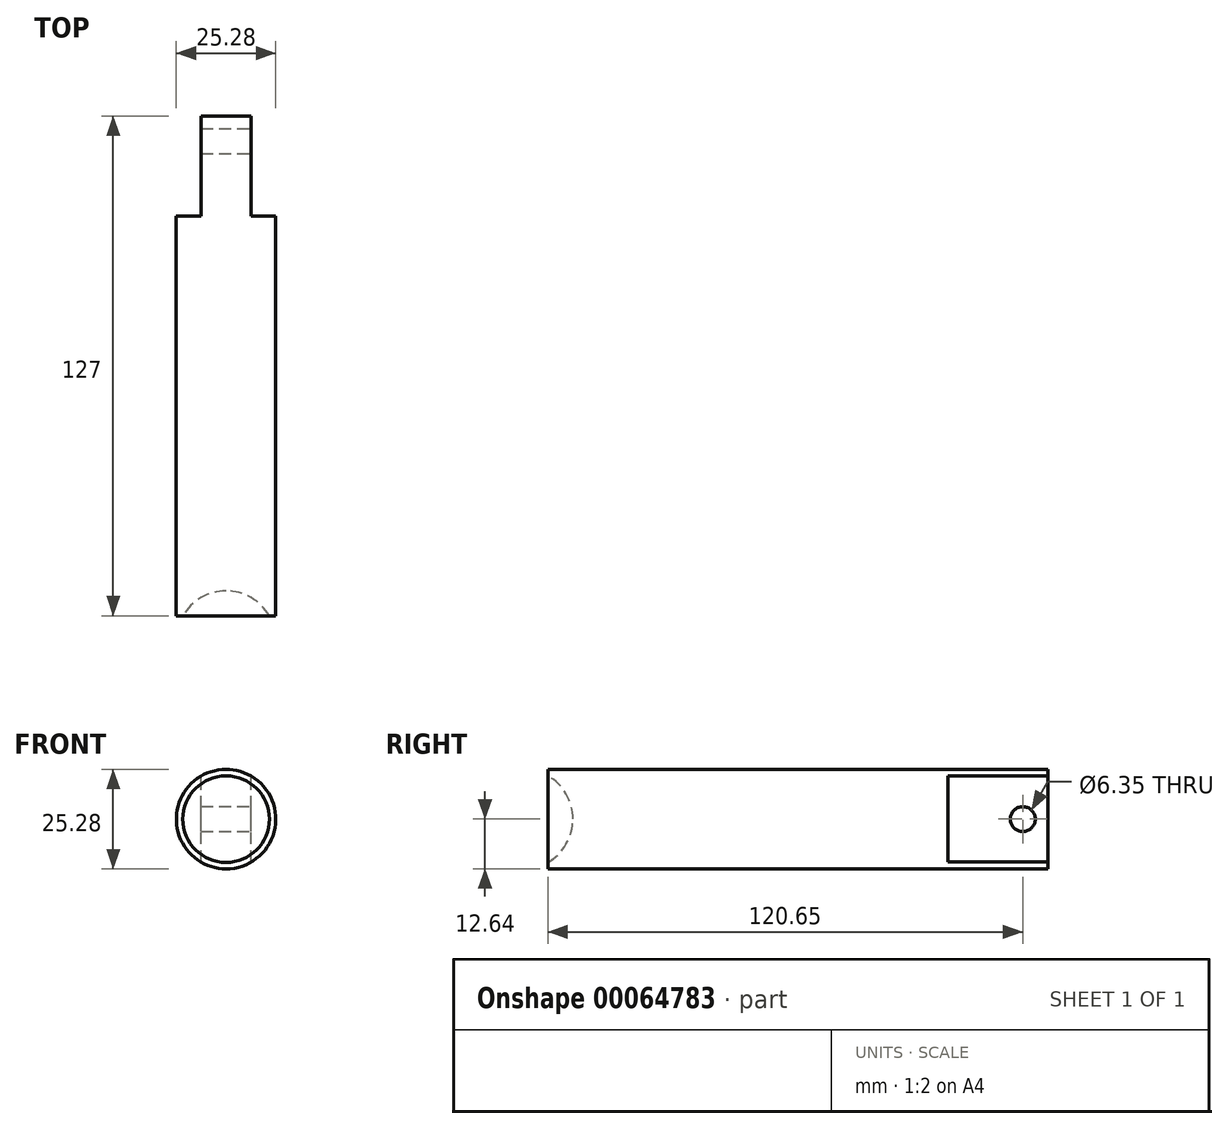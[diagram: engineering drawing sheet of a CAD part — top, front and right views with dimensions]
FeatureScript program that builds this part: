
annotation { "Feature Type Name" : "Feature", "Feature Type Description" : "" }
export const myFeature = defineFeature(function(context is Context, id is Id, definition is map)
    precondition{}
    {
        {
            var Q0;
            Q0=qCreatedBy(makeId("Front.planeOp"),FACE);
            var sketch = newSketch(context, id + "F0", { "sketchPlane" : qUnion([Q0])});
            skCircle(sketch, "E0", {"center": v(0, 0) * mm, "radius": 12.64 * mm});
            skSolve(sketch);
        }
        {
            var Q0;
            Q0=makeQuery(id+"F0.imprint","IMPRINT",FACE,{"disambiguationData":[TD([[makeQuery(id+"F0.imprint","IMPRINT",EDGE,{"derivedFrom":sQuery(id+"F0.wireOp",EDGE,"E0")}),1.0]])]});
            extrude(context, id + "F1", {"entities" : qUnion([Q0]), "depth" : 127 * mm});
        }
        {
            var Q0;
            Q0=qCreatedBy(makeId("Right.planeOp"),FACE);
            var sketch = newSketch(context, id + "F2", { "sketchPlane" : qUnion([Q0])});
            skArc(sketch, "E1", {"start": v(-120.65, 0) * mm, "mid": v(-124.37, 8.98) * mm, "end": v(-133.35, 12.7) * mm});
            skLineSegment(sketch, "E2", {"start": v(-133.35, 0) * mm, "end": v(-133.35, 12.7) * mm});
            skLineSegment(sketch, "E3", {"start": v(-133.35, 0) * mm, "end": v(-120.65, 0) * mm});
            skSolve(sketch);
        }
        {
            var Q0;
            Q0=makeQuery(id+"F2.imprint","IMPRINT",FACE,{"disambiguationData":[TD([[makeQuery(id+"F2.imprint","IMPRINT",EDGE,{"derivedFrom":sQuery(id+"F2.wireOp",EDGE,"E1")}),1.0]])]});
            var Q1;
            Q1=sQuery(id+"F2.wireOp",EDGE,"E3");
            revolve(context, id + "F3", {"operationType" : NewBodyOperationType.REMOVE, "entities" : qUnion([Q0]), "axis" : qUnion([Q1]), "revolveType" : RevolveType.FULL, "oppositeDirection" : true});
        }
        {
            var Q0;
            Q0=qCreatedBy(makeId("Top.planeOp"),FACE);
            var sketch = newSketch(context, id + "F4", { "sketchPlane" : qUnion([Q0])});
            skLineSegment(sketch, "E4.bottom", {"start": v(-34.18, -25.4) * mm, "end": v(-6.35, -25.4) * mm});
            skLineSegment(sketch, "E4.top", {"start": v(-34.18, 25.67) * mm, "end": v(-6.35, 25.67) * mm});
            skLineSegment(sketch, "E4.left", {"start": v(-34.18, -25.4) * mm, "end": v(-34.18, 25.67) * mm});
            skLineSegment(sketch, "E4.right", {"start": v(-6.35, -25.4) * mm, "end": v(-6.35, 25.67) * mm});
            skLineSegment(sketch, "E5.bottom", {"start": v(6.35, -25.4) * mm, "end": v(31.48, -25.4) * mm});
            skLineSegment(sketch, "E5.top", {"start": v(6.35, 19.75) * mm, "end": v(31.48, 19.75) * mm});
            skLineSegment(sketch, "E5.left", {"start": v(6.35, -25.4) * mm, "end": v(6.35, 19.75) * mm});
            skLineSegment(sketch, "E5.right", {"start": v(31.48, -25.4) * mm, "end": v(31.48, 19.75) * mm});
            skSolve(sketch);
        }
        {
            var Q0;
            Q0=qSketchRegion(id+"F4",true);
            extrude(context, id + "F5", {"entities" : qUnion([Q0]), "operationType" : NewBodyOperationType.REMOVE, "endBound" : BoundingType.THROUGH_ALL, "oppositeDirection" : true, "depth" : 25.4 * mm, "hasSecondDirection" : true, "secondDirectionOppositeDirection" : false, "secondDirectionDepth" : 25.4 * mm});
        }
        {
            var Q0;
            Q0=qCreatedBy(makeId("Right.planeOp"),FACE);
            var sketch = newSketch(context, id + "F6", { "sketchPlane" : qUnion([Q0])});
            skCircle(sketch, "E6", {"center": v(-6.35, 0) * mm, "radius": 3.18 * mm});
            skSolve(sketch);
        }
        {
            var Q0;
            Q0=qSketchRegion(id+"F6",true);
            extrude(context, id + "F7", {"entities" : qUnion([Q0]), "operationType" : NewBodyOperationType.REMOVE, "endBound" : BoundingType.THROUGH_ALL, "oppositeDirection" : true, "depth" : 25.4 * mm, "hasSecondDirection" : true, "secondDirectionOppositeDirection" : false, "secondDirectionDepth" : 25.4 * mm});
        }
    });
